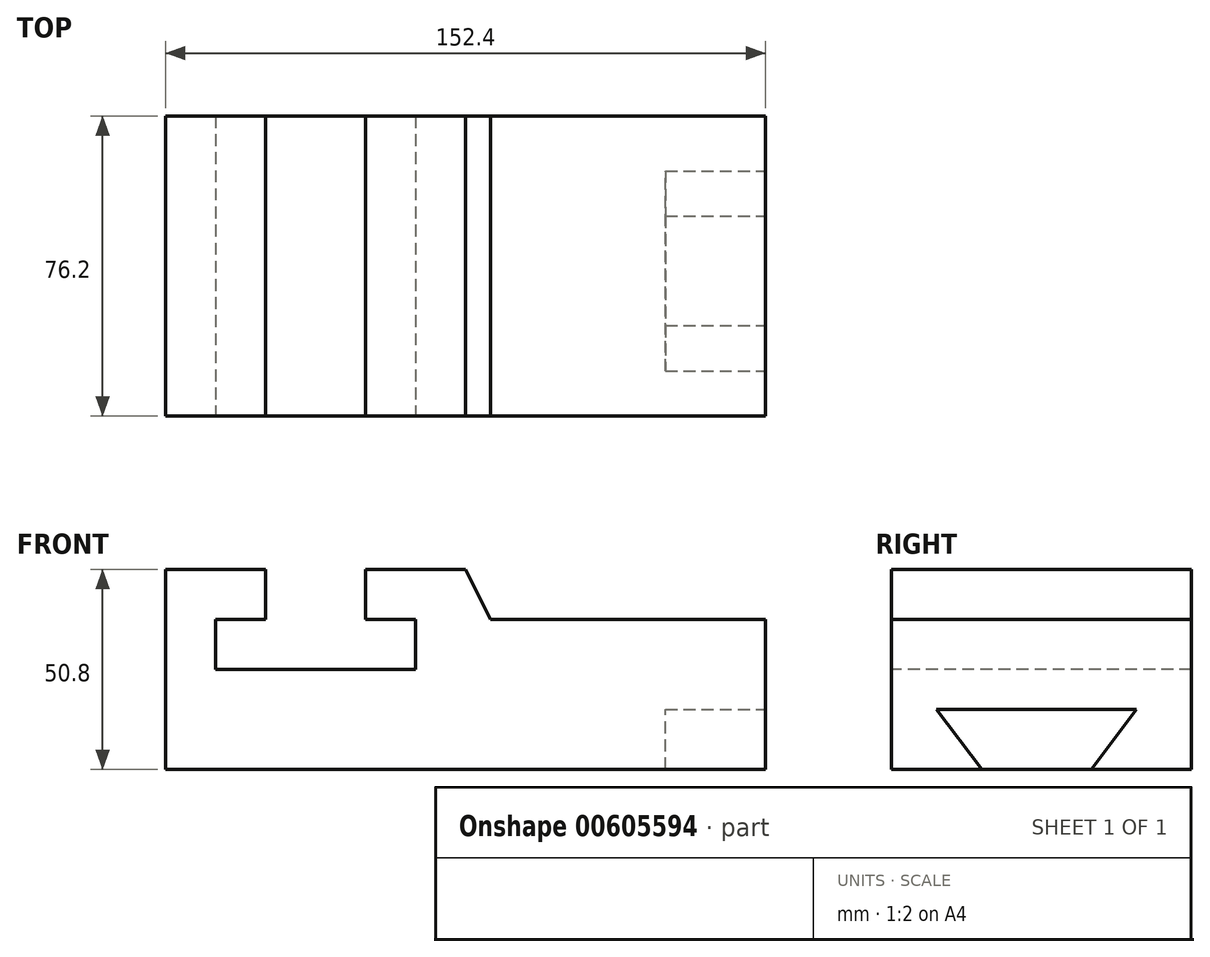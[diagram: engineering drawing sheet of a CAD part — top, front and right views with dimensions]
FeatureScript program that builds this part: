
annotation { "Feature Type Name" : "Feature", "Feature Type Description" : "" }
export const myFeature = defineFeature(function(context is Context, id is Id, definition is map)
    precondition{}
    {
        {
            var Q0;
            Q0=qCreatedBy(makeId("Front.planeOp"),FACE);
            var sketch = newSketch(context, id + "F0", { "sketchPlane" : qUnion([Q0])});
            skLineSegment(sketch, "E0", {"start": v(135.6, 12.7) * mm, "end": v(135.6, 25.4) * mm});
            skLineSegment(sketch, "E1", {"start": v(135.6, 25.4) * mm, "end": v(110.2, 25.4) * mm});
            skLineSegment(sketch, "E2", {"start": v(110.2, 25.4) * mm, "end": v(110.2, -25.4) * mm});
            skLineSegment(sketch, "E3", {"start": v(110.2, -25.4) * mm, "end": v(262.6, -25.4) * mm});
            skLineSegment(sketch, "E4", {"start": v(262.6, -25.4) * mm, "end": v(262.6, 12.7) * mm});
            skLineSegment(sketch, "E5", {"start": v(262.6, 12.7) * mm, "end": v(192.74, 12.7) * mm});
            skLineSegment(sketch, "E6", {"start": v(192.74, 12.7) * mm, "end": v(186.4, 25.4) * mm});
            skLineSegment(sketch, "E7", {"start": v(186.4, 25.4) * mm, "end": v(161, 25.4) * mm});
            skLineSegment(sketch, "E8", {"start": v(161, 25.4) * mm, "end": v(161, 12.7) * mm});
            skLineSegment(sketch, "E9", {"start": v(161, 12.7) * mm, "end": v(173.7, 12.7) * mm});
            skLineSegment(sketch, "E10", {"start": v(173.7, 12.7) * mm, "end": v(173.7, 0) * mm});
            skLineSegment(sketch, "E11", {"start": v(173.7, 0) * mm, "end": v(122.9, 0) * mm});
            skLineSegment(sketch, "E12", {"start": v(122.9, 0) * mm, "end": v(122.9, 12.7) * mm});
            skLineSegment(sketch, "E13", {"start": v(122.9, 12.7) * mm, "end": v(135.6, 12.7) * mm});
            skSolve(sketch);
        }
        {
            var Q0;
            Q0=makeQuery(id+"F0.imprint","IMPRINT",FACE,{"disambiguationData":[TD([[makeQuery(id+"F0.imprint","IMPRINT",EDGE,{"derivedFrom":sQuery(id+"F0.wireOp",EDGE,"E0")}),1.0]])]});
            extrude(context, id + "F1", {"entities" : qUnion([Q0]), "oppositeDirection" : true, "depth" : 76.2 * mm, "offsetDistance" : 25.4 * mm});
        }
        {
            var Q0;
            Q0=makeQuery(id+"F1.opExtrude","SWEPT_FACE",FACE,{"disambiguationData":[OSD([sQuery(id+"F0.wireOp",EDGE,"E4")])]});
            var sketch = newSketch(context, id + "F2", { "sketchPlane" : qUnion([Q0])});
            skLineSegment(sketch, "E14", {"start": v(0, -25.4) * mm, "end": v(22.97, -25.4) * mm});
            skLineSegment(sketch, "E15", {"start": v(22.97, -25.4) * mm, "end": v(11.48, -10.2) * mm});
            skLineSegment(sketch, "E16", {"start": v(11.48, -10.2) * mm, "end": v(62.28, -10.2) * mm});
            skLineSegment(sketch, "E17", {"start": v(62.28, -10.2) * mm, "end": v(50.8, -25.4) * mm});
            skLineSegment(sketch, "E18", {"start": v(50.8, -25.4) * mm, "end": v(76.2, -25.4) * mm});
            skSolve(sketch);
        }
        {
            var Q0;
            {var subQ0=sQuery(id+"F2.wireOp",EDGE,"E15");Q0=makeQuery(id+"F2.imprint","IMPRINT",FACE,{"disambiguationData":[TD([[makeQuery(id+"F2.imprint","IMPRINT",EDGE,{"derivedFrom":subQ0}),-1.0]])]});}
            extrude(context, id + "F3", {"entities" : qUnion([Q0]), "operationType" : NewBodyOperationType.REMOVE, "oppositeDirection" : true, "depth" : 25.4 * mm, "offsetDistance" : 25.4 * mm});
        }
    });
